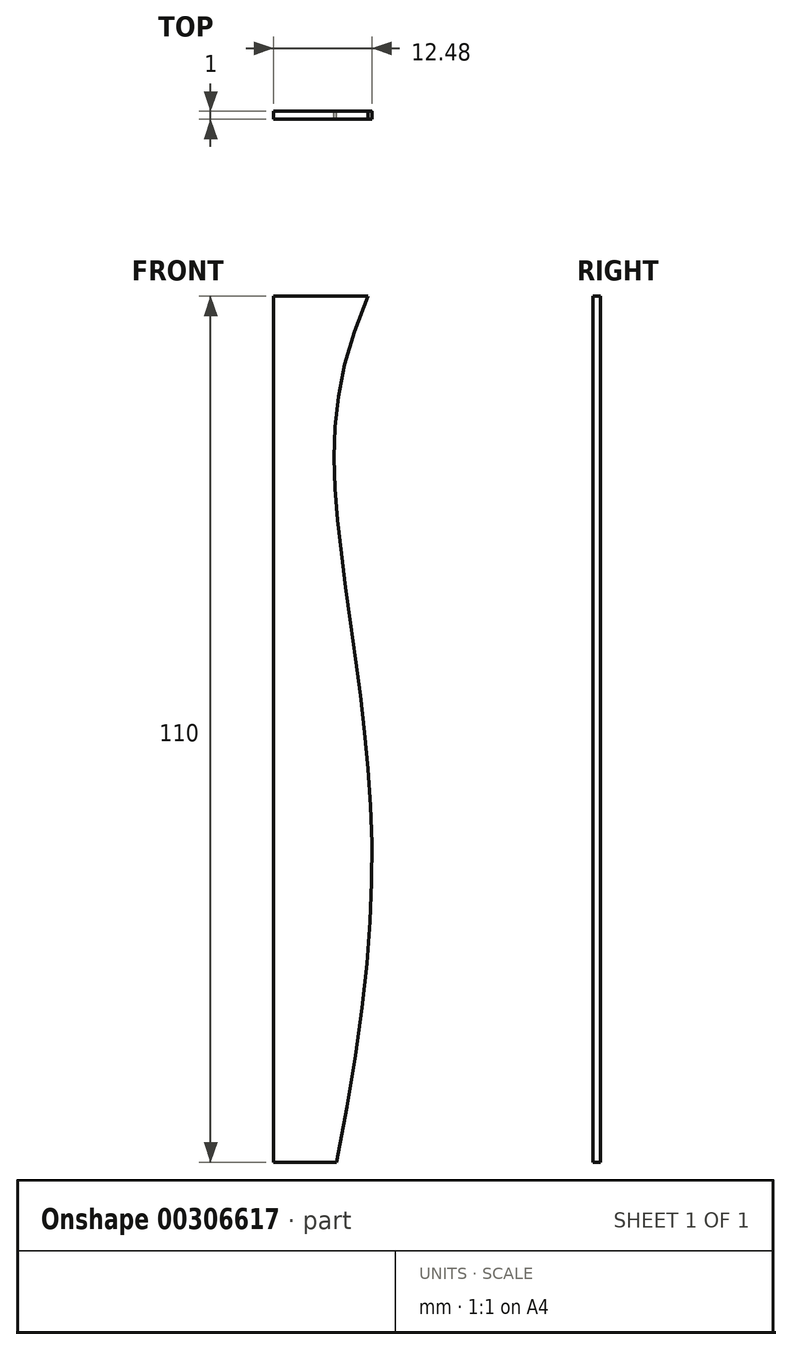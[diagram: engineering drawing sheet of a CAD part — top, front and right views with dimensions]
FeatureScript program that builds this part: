
annotation { "Feature Type Name" : "Feature", "Feature Type Description" : "" }
export const myFeature = defineFeature(function(context is Context, id is Id, definition is map)
    precondition{}
    {
        {
            var Q0;
            Q0=qCreatedBy(makeId("Front.planeOp"),FACE);
            var sketch = newSketch(context, id + "F0", { "sketchPlane" : qUnion([Q0])});
            skLineSegment(sketch, "E0", {"start": v(0, 0) * mm, "end": v(8, 0) * mm});
            skFitSpline(sketch, "E1", {"points": [v(8, 0) * mm, v(12, 50) * mm, v(8, 83) * mm, v(12, 110) * mm], "startDerivative": vector(33.5, 168.85) * mm, "endDerivative": vector(46.04, 107.03) * mm});
            skLineSegment(sketch, "E2", {"start": v(12, 110) * mm, "end": v(0, 110) * mm});
            skLineSegment(sketch, "E3", {"start": v(0, 110) * mm, "end": v(0, 0) * mm});
            skSolve(sketch);
        }
        {
            var Q0;
            Q0=makeQuery(id+"F0.imprint","IMPRINT",FACE,{"disambiguationData":[TD([[makeQuery(id+"F0.imprint","IMPRINT",EDGE,{"derivedFrom":sQuery(id+"F0.wireOp",EDGE,"E0")}),1.0]])]});
            extrude(context, id + "F1", {"entities" : qUnion([Q0]), "depth" : 1 * mm});
        }
    });
